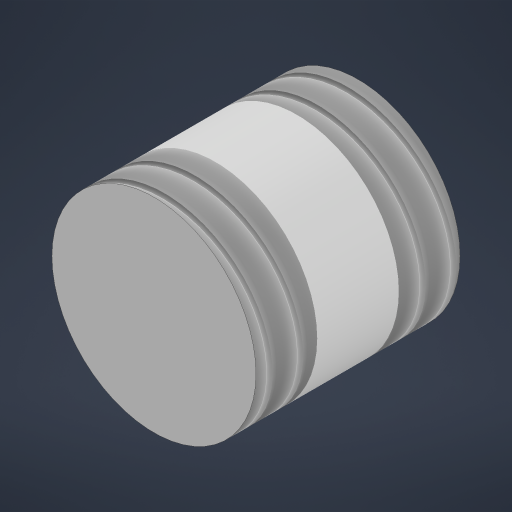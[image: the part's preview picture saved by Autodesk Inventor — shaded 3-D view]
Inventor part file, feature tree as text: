
AUTODESK INVENTOR PART (.ipt)
format: ipt  version: 2023 (Build 270158000, 158)  size: 205,312 bytes
history: native  units: mm
features: thread x2, extrude x1, sketch x1
ambient origin geometry x8: Origin, YZ Plane, XZ Plane, XY Plane, X Axis, Y Axis, Z Axis, Center Point
bodies: Solid1 (feature_tree)
feature tree (4):
  extrude  "Extrusion1"  Depth=10.0mm TaperAngle=0.0deg
  thread  "Thread1"  [1 undecoded]
  thread  "Thread2"  [1 undecoded]
  sketch  "Sketch1"  dims[d0=10.0mm d1=10.0mm d2=0.0mm d3=3.0mm d4=0.0mm d5=3.0mm d6=0.0mm]
note: 2 required parameter values undecoded (feature->parameter linkage not recoverable at this tier; creation-order binding heuristic only, values carry confidence <= 0.55)
